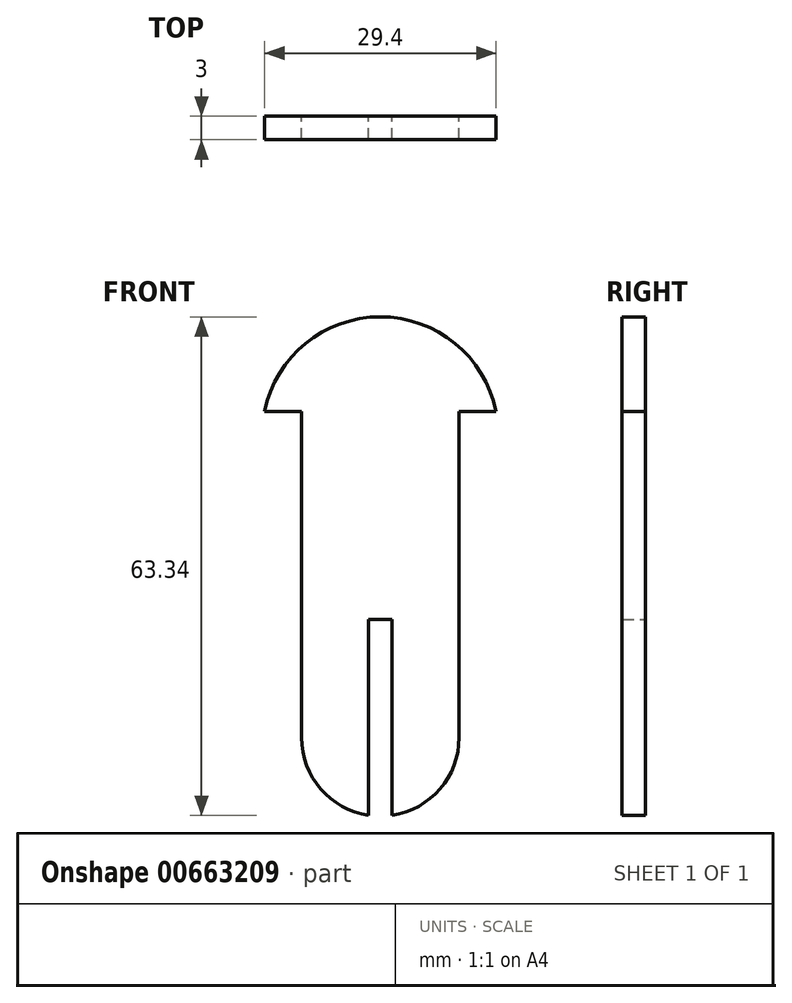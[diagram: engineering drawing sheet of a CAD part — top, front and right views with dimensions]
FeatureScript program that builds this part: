
annotation { "Feature Type Name" : "Feature", "Feature Type Description" : "" }
export const myFeature = defineFeature(function(context is Context, id is Id, definition is map)
    precondition{}
    {
        {
            var Q0;
            Q0=qCreatedBy(makeId("Front.planeOp"),FACE);
            var sketch = newSketch(context, id + "F0", { "sketchPlane" : qUnion([Q0])});
            skLineSegment(sketch, "E0", {"start": v(-10, 41.45) * mm, "end": v(-10, 0) * mm});
            skLineSegment(sketch, "E1", {"start": v(-1.5, -9.89) * mm, "end": v(-1.5, 15) * mm});
            skLineSegment(sketch, "E2", {"start": v(-1.5, 15) * mm, "end": v(1.5, 15) * mm});
            skLineSegment(sketch, "E3", {"start": v(1.5, 15) * mm, "end": v(1.5, -9.89) * mm});
            skArc(sketch, "E4", {"start": v(14.7, 41.45) * mm, "mid": v(0, 53.45) * mm, "end": v(-14.7, 41.45) * mm});
            skLineSegment(sketch, "E5", {"start": v(-14.7, 41.45) * mm, "end": v(-10, 41.45) * mm});
            skLineSegment(sketch, "E6", {"start": v(10, 41.45) * mm, "end": v(14.7, 41.45) * mm});
            skLineSegment(sketch, "E7", {"start": v(-10, 0) * mm, "end": v(-10, 0) * mm});
            skLineSegment(sketch, "E8", {"start": v(10, 41.45) * mm, "end": v(10, 0) * mm});
            skArc(sketch, "E9", {"start": v(10, 0) * mm, "mid": v(7.58, -6.52) * mm, "end": v(1.5, -9.89) * mm});
            skArc(sketch, "E10", {"start": v(-10, 0) * mm, "mid": v(-7.58, -6.52) * mm, "end": v(-1.5, -9.89) * mm});
            skSolve(sketch);
        }
        {
            var Q0;
            Q0=qSketchRegion(id+"F0",true);
            extrude(context, id + "F1", {"entities" : qUnion([Q0]), "depth" : 3 * mm, "offsetDistance" : 25 * mm});
        }
    });
